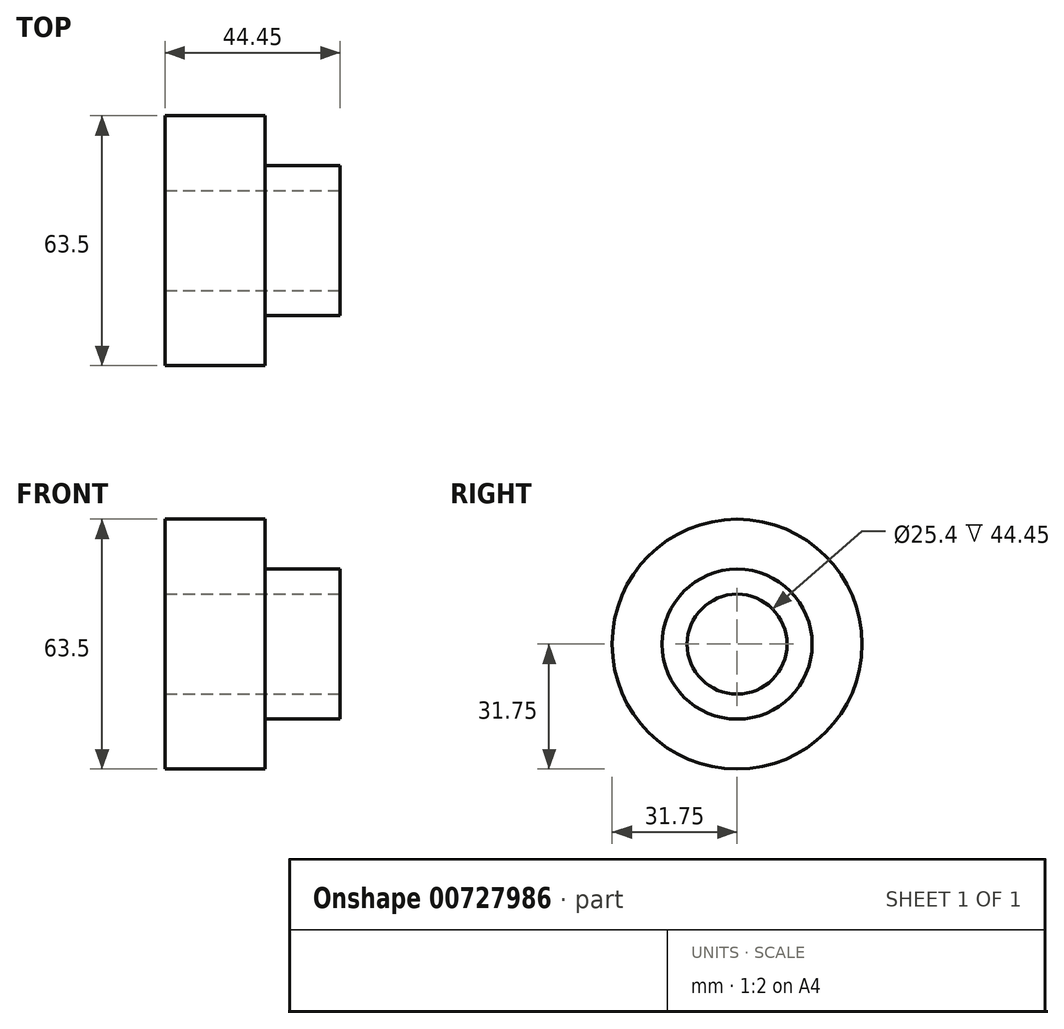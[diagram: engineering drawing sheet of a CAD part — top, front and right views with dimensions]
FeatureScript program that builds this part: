
annotation { "Feature Type Name" : "Feature", "Feature Type Description" : "" }
export const myFeature = defineFeature(function(context is Context, id is Id, definition is map)
    precondition{}
    {
        {
            var Q0;
            Q0=qCreatedBy(makeId("Right.planeOp"),FACE);
            var sketch = newSketch(context, id + "F0", { "sketchPlane" : qUnion([Q0])});
            skCircle(sketch, "E0", {"center": v(0, 0) * mm, "radius": 31.75 * mm});
            skSolve(sketch);
        }
        {
            var Q0;
            Q0 = qSketchRegion(id + "F0", true);
            extrude(context, id + "F1", {"entities" : qUnion([Q0]), "depth" : 25.4 * mm, "offsetDistance" : 25.4 * mm});
        }
        {
            var Q0;
            Q0=makeQuery(id+"F1.opExtrude","CAP_FACE",FACE,{"disambiguationData":[OSD([sQuery(id+"F0.wireOp",EDGE,"E0")])],"isStart":false});
            var sketch = newSketch(context, id + "F2", { "sketchPlane" : qUnion([Q0])});
            skCircle(sketch, "E1", {"center": v(0, 0) * mm, "radius": 19.05 * mm});
            skSolve(sketch);
        }
        {
            var Q0;
            Q0 = qSketchRegion(id + "F2", true);
            extrude(context, id + "F3", {"entities" : qUnion([Q0]), "operationType" : NewBodyOperationType.ADD, "depth" : 19.05 * mm, "offsetDistance" : 25.4 * mm});
        }
        {
            var Q0;
            Q0=makeQuery(id+"F3.opExtrude","CAP_FACE",FACE,{"disambiguationData":[OSD([sQuery(id+"F2.wireOp",EDGE,"E1")])],"isStart":false});
            var sketch = newSketch(context, id + "F4", { "sketchPlane" : qUnion([Q0])});
            skCircle(sketch, "E2", {"center": v(0, 0) * mm, "radius": 12.7 * mm});
            skSolve(sketch);
        }
        {
            var Q0;
            Q0 = qSketchRegion(id + "F4", true);
            extrude(context, id + "F5", {"entities" : qUnion([Q0]), "operationType" : NewBodyOperationType.REMOVE, "oppositeDirection" : true, "depth" : 177.8 * mm, "offsetDistance" : 25.4 * mm});
        }
    });
